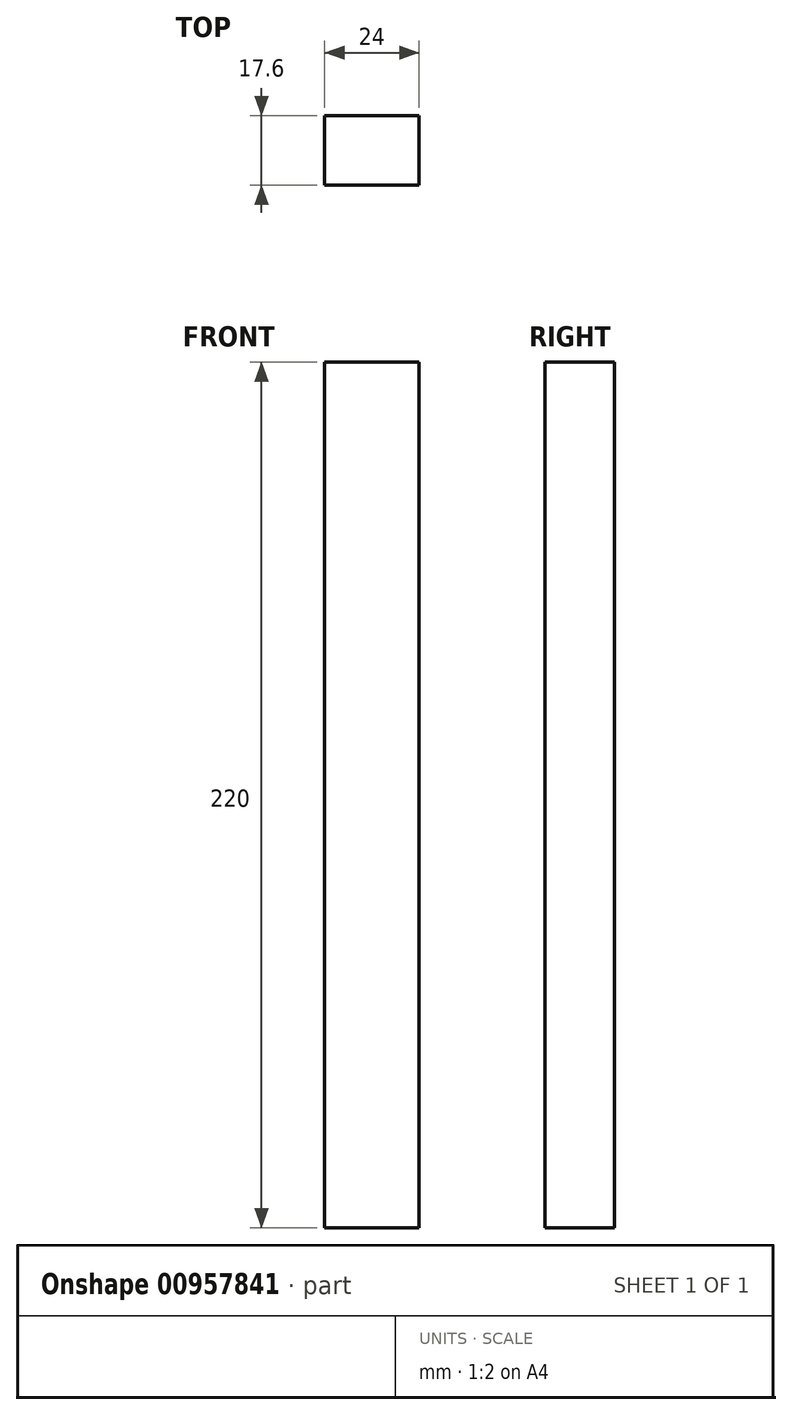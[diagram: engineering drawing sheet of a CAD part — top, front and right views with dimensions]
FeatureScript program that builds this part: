
annotation { "Feature Type Name" : "Feature", "Feature Type Description" : "" }
export const myFeature = defineFeature(function(context is Context, id is Id, definition is map)
    precondition{}
    {
        {
            var Q0;
            Q0=qCreatedBy(makeId("Top.planeOp"),FACE);
            var sketch = newSketch(context, id + "F0", { "sketchPlane" : qUnion([Q0])});
            skLineSegment(sketch, "E0.bottom", {"start": v(-11.51, 9.04) * mm, "end": v(12.49, 9.04) * mm});
            skLineSegment(sketch, "E0.top", {"start": v(-11.51, -8.56) * mm, "end": v(12.49, -8.56) * mm});
            skLineSegment(sketch, "E0.left", {"start": v(-11.51, 9.04) * mm, "end": v(-11.51, -8.56) * mm});
            skLineSegment(sketch, "E0.right", {"start": v(12.49, 9.04) * mm, "end": v(12.49, -8.56) * mm});
            skSolve(sketch);
        }
        {
            var Q0;
            Q0=makeQuery(id+"F0.imprint","IMPRINT",FACE,{"disambiguationData":[TD([[makeQuery(id+"F0.imprint","IMPRINT",EDGE,{"derivedFrom":sQuery(id+"F0.wireOp",EDGE,"E0.bottom")}),-1.0]])]});
            extrude(context, id + "F1", {"entities" : qUnion([Q0]), "depth" : 220 * mm, "offsetDistance" : 25 * mm});
        }
    });
